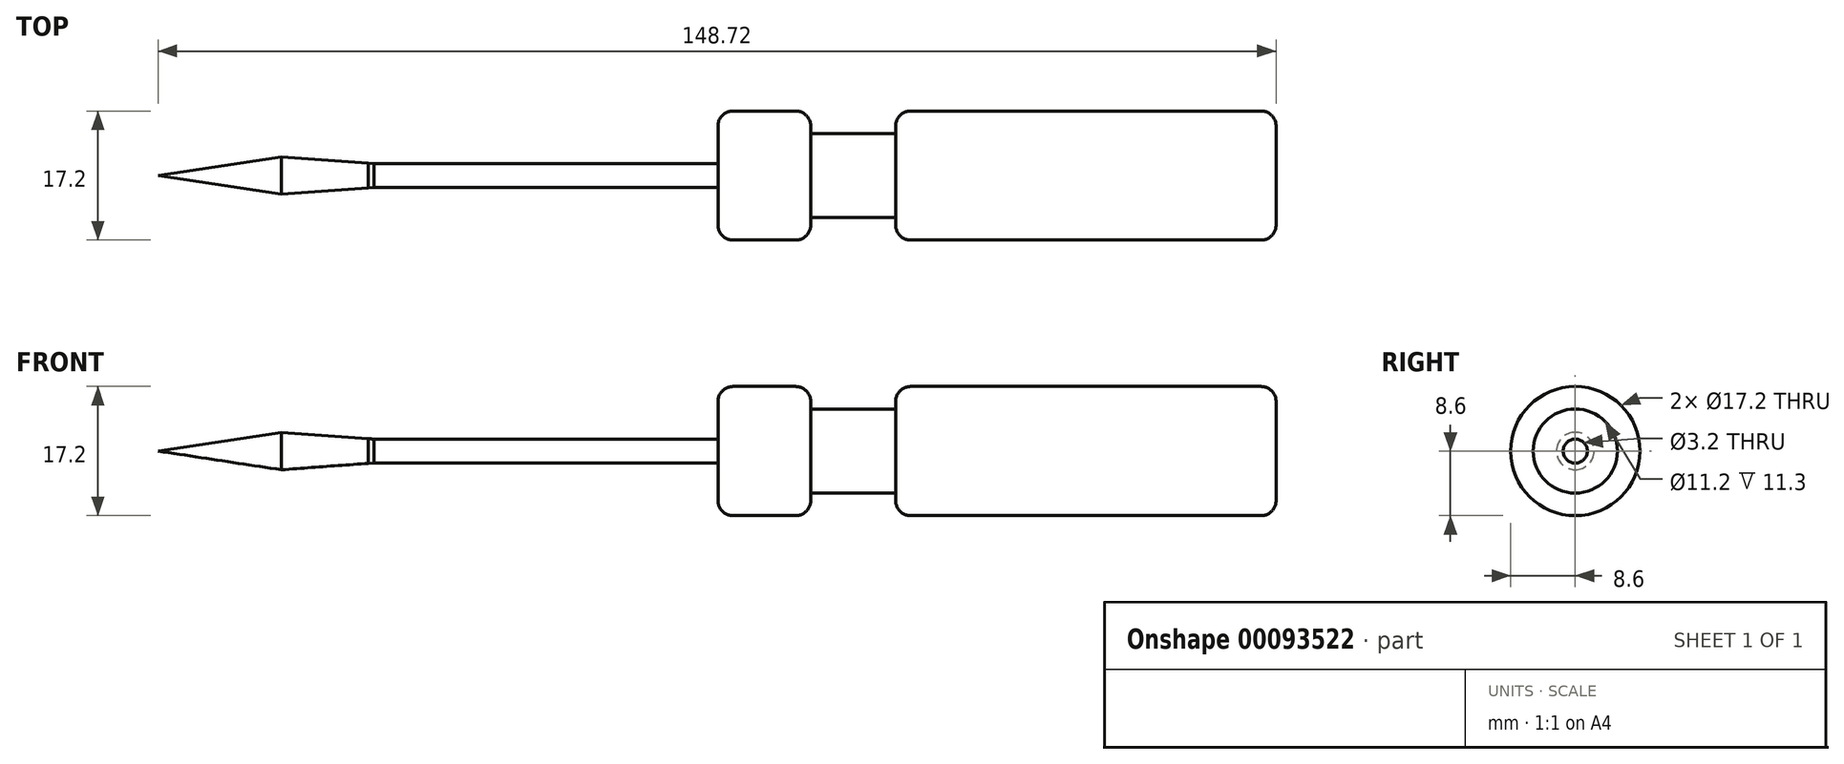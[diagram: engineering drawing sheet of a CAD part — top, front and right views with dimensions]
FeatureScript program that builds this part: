
annotation { "Feature Type Name" : "Feature", "Feature Type Description" : "" }
export const myFeature = defineFeature(function(context is Context, id is Id, definition is map)
    precondition{}
    {
        {
            var Q0;
            Q0=qCreatedBy(makeId("Front.planeOp"),FACE);
            var sketch = newSketch(context, id + "F0", { "sketchPlane" : qUnion([Q0])});
            skLineSegment(sketch, "E0", {"start": v(79.6, 0) * mm, "end": v(-69.12, 0) * mm, "construction": true});
            skLineSegment(sketch, "E1", {"start": v(79.6, 0) * mm, "end": v(79.6, 8.6) * mm});
            skLineSegment(sketch, "E2", {"start": v(79.6, 8.6) * mm, "end": v(29, 8.6) * mm});
            skLineSegment(sketch, "E3", {"start": v(29, 8.6) * mm, "end": v(29, 5.6) * mm});
            skLineSegment(sketch, "E4", {"start": v(29, 5.6) * mm, "end": v(17.7, 5.6) * mm});
            skLineSegment(sketch, "E5", {"start": v(17.7, 5.6) * mm, "end": v(17.7, 8.6) * mm});
            skLineSegment(sketch, "E6", {"start": v(17.7, 8.6) * mm, "end": v(5.36, 8.6) * mm});
            skLineSegment(sketch, "E7", {"start": v(5.36, 8.6) * mm, "end": v(5.36, 1.6) * mm});
            skLineSegment(sketch, "E8", {"start": v(5.36, 1.6) * mm, "end": v(-40.76, 1.6) * mm});
            skLineSegment(sketch, "E9", {"start": v(-40.76, 1.6) * mm, "end": v(-52.72, 2.5) * mm});
            skLineSegment(sketch, "E10", {"start": v(-52.72, 2.5) * mm, "end": v(-69.12, 0) * mm});
            skSolve(sketch);
        }
        {
            var Q0;
            Q0=sQuery(id+"F0.wireOp",EDGE,"E1");
            var Q1;
            Q1=sQuery(id+"F0.wireOp",EDGE,"E2");
            var Q2;
            Q2=sQuery(id+"F0.wireOp",EDGE,"E3");
            var Q3;
            Q3=sQuery(id+"F0.wireOp",EDGE,"E4");
            var Q4;
            Q4=sQuery(id+"F0.wireOp",EDGE,"E5");
            var Q5;
            Q5=sQuery(id+"F0.wireOp",EDGE,"E6");
            var Q6;
            Q6=sQuery(id+"F0.wireOp",EDGE,"E7");
            var Q7;
            Q7=sQuery(id+"F0.wireOp",EDGE,"E8");
            var Q8;
            Q8=sQuery(id+"F0.wireOp",EDGE,"E9");
            var Q9;
            Q9=sQuery(id+"F0.wireOp",EDGE,"E10");
            var Q10;
            Q10=sQuery(id+"F0.wireOp",EDGE,"E0");
            revolve(context, id + "F1", {"bodyType" : ToolBodyType.SURFACE, "surfaceEntities" : qUnion([Q0, Q1, Q2, Q3, Q4, Q5, Q6, Q7, Q8, Q9]), "axis" : qUnion([Q10]), "revolveType" : RevolveType.FULL});
        }
        {
            var Q0;
            Q0=makeQuery(id+"F1.opRevolve","SWEPT_EDGE",EDGE,{"disambiguationData":[OSD([sQuery(id+"F0.wireOp",VERTEX,"E7.start")])]});
            var Q1;
            Q1=makeQuery(id+"F1.opRevolve","SWEPT_EDGE",EDGE,{"disambiguationData":[OSD([sQuery(id+"F0.wireOp",VERTEX,"E6.start")])]});
            var Q2;
            Q2=makeQuery(id+"F1.opRevolve","SWEPT_EDGE",EDGE,{"disambiguationData":[OSD([sQuery(id+"F0.wireOp",VERTEX,"E3.start")])]});
            var Q3;
            Q3=makeQuery(id+"F1.opRevolve","SWEPT_EDGE",EDGE,{"disambiguationData":[OSD([sQuery(id+"F0.wireOp",VERTEX,"E2.start")])]});
            fillet(context, id + "F2", {"entities" : qUnion([Q0, Q1, Q2, Q3]), "radius" : 2 * mm, "tangentPropagation" : true, "allowEdgeOverflow" : false});
        }
        {
            var Q0;
            Q0=makeQuery(id+"F1.opRevolve","SWEPT_EDGE",EDGE,{"disambiguationData":[OSD([sQuery(id+"F0.wireOp",VERTEX,"E9.start")])]});
            chamfer(context, id + "F3", {"entities" : qUnion([Q0]), "width" : 10 * mm, "tangentPropagation" : true});
        }
    });
